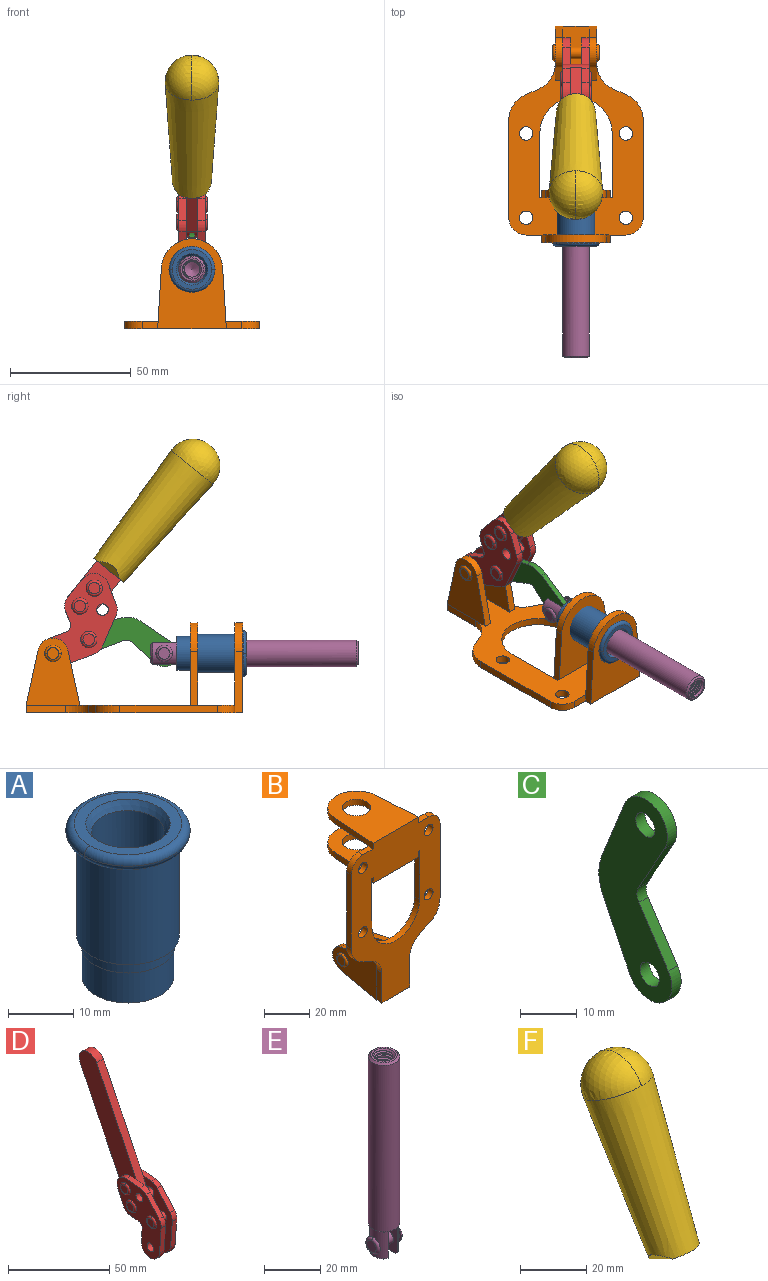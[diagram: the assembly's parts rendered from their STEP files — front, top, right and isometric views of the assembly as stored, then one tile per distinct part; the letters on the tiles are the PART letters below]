
ASSEMBLY  parts=6 mates=6
PART A: 15 faces, bbox 20.6x20.6x28.7 mm
  f0: torus R=8.26mm, axis (0,0,1), area 56.8mm2, adj f1,f10,f12
  f1: torus R=8.26mm, axis (0,0,1), area 56.8mm2, adj f0,f6,f13
  f2: cylinder r=5.59mm len=25.91mm, axis (0,0,1), area 909.6mm2, adj f3,f4
  f3: cone r=6.86mm half-angle=45deg, axis (0,0,-1), area 70.2mm2, adj f2,f14
  f4: cone r=6.47mm half-angle=30deg, axis (0,0,1), area 66.7mm2, adj f2,f13
  f5: cylinder r=7.04mm len=14.07mm, axis (0,0,1), area 252.6mm2, adj f11,f14
  f6: torus R=8.26mm, axis (0,0,1), area 56.8mm2, adj f1,f12,f13
  f7: cylinder r=7.16mm len=14.33mm, axis (0,0,1), area 91.5mm2, adj f9,f11
  f8: cylinder r=7.86mm len=18.42mm, axis (0,0,1), area 909.6mm2, adj f9,f10
  f9: plane 15.72x15.72mm, normal (0,0,-1), area 33mm2, adj f7,f8
  f10: plane 16.51x16.51mm, normal (0,0,-1), area 19.9mm2, adj f0,f8,f12
  f11: plane 14.33x14.33mm, normal (0,0,-1), area 5.7mm2, adj f5,f7
  f12: torus R=8.26mm, axis (0,0,1), area 56.8mm2, adj f0,f6,f10
  f13: plane 16.51x16.51mm, normal (0,0,1), area 82.7mm2, adj f1,f4,f6
  f14: plane 14.07x14.07mm, normal (0,0,-1), area 7.8mm2, adj f3,f5
PART B: 55 faces, bbox 55.7x37.4x89.8 mm
  f0: torus R=2.41mm, axis (-1,0,0), area 15mm2, adj f11,f15,f25
  f1: torus R=2.41mm, axis (-1,0,0), area 15mm2, adj f10,f12,f22
  f2: cylinder r=2.78mm len=5.56mm, axis (0,-1,0), area 54.2mm2, adj f30,f54
  f3: cylinder r=14.99mm len=29.97mm, axis (0,-1,0), area 145.9mm2, adj f30,f49,f53,f54
  f4: cylinder r=2.78mm len=5.56mm, axis (0,-1,0), area 54.2mm2, adj f30,f54
  f5: cylinder r=2.78mm len=5.56mm, axis (0,-1,0), area 54.2mm2, adj f30,f54
  f6: cylinder r=2.78mm len=5.56mm, axis (0,-1,0), area 54.2mm2, adj f30,f54
  f7: cylinder r=6.35mm len=12.7mm, axis (0,0,1), area 123.6mm2, adj f27,f51
  f8: cylinder r=6.35mm len=12.7mm, axis (0,0,-1), area 124.7mm2, adj f21,f35
  f9: cylinder r=2.41mm len=11.18mm, axis (-1,0,0), area 169.4mm2, adj f16,f19
  f10: plane 4.83x4.83mm, normal (1,0,0), area 18.3mm2, adj f1,f12
  f11: plane 4.83x4.83mm, normal (-1,0,0), area 18.3mm2, adj f0,f15
  f12: torus R=2.41mm, axis (-1,0,0), area 15mm2, adj f1,f10,f22
  f13: cylinder r=6.35mm len=12.41mm, axis (1,0,0), area 53.4mm2, adj f18,f19,f22,f23
  f14: cylinder r=6.35mm len=12.41mm, axis (-1,0,0), area 53.4mm2, adj f16,f17,f24,f25
  f15: torus R=2.41mm, axis (-1,0,0), area 15mm2, adj f0,f11,f25
  f16: plane 27.86x22.35mm, normal (1,0,0), area 425.4mm2, adj f9,f14,f17,f24,f30
  f17: plane 22.86x4.97mm, normal (0,0.21,0.98), area 72.5mm2, adj f14,f16,f25,f30
  f18: plane 22.86x4.97mm, normal (0,0.21,0.98), area 72.5mm2, adj f13,f19,f22,f30
  f19: plane 27.86x22.35mm, normal (-1,0,0), area 425.4mm2, adj f9,f13,f18,f23,f30
  f20: cylinder r=12.7mm len=25.35mm, axis (0,0,-1), area 119.8mm2, adj f21,f34,f35,f36
  f21: plane 34.21x28.07mm, normal (0,0,-1), area 702.4mm2, adj f8,f20,f30,f34,f36
  f22: plane 27.96x22.45mm, normal (1,0,0), area 407.2mm2, adj f1,f12,f13,f18,f23,f30,f42,f43
  f23: plane 22.86x4.97mm, normal (0,0.21,-0.98), area 72.5mm2, adj f13,f19,f22,f44
  f24: plane 22.86x4.97mm, normal (0,0.21,-0.98), area 72.5mm2, adj f14,f16,f25,f44
  f25: plane 27.86x22.35mm, normal (-1,0,0), area 407.1mm2, adj f0,f14,f15,f17,f24,f30,f45,f46
  f26: plane 3.1x0.95mm, normal (0,0,-1), area 2.7mm2, adj f30,f49,f50,f54
  f27: plane 34.21x28.07mm, normal (0,0,1), area 702.4mm2, adj f7,f28,f30,f50,f52
  f28: cylinder r=12.7mm len=25.35mm, axis (0,0,1), area 118.8mm2, adj f27,f50,f51,f52
  f29: plane 3.1x0.95mm, normal (0,0,-1), area 2.7mm2, adj f30,f52,f53,f54
  f30: plane 86.54x55.63mm, normal (0,1,0), area 2362.9mm2, adj f2,f3,f4,f5,f6,f16,f17,f18
  f31: plane 40.56x3.1mm, normal (-1,0,0), area 125.7mm2, adj f30,f32,f48,f54
  f32: cylinder r=7.11mm len=7.11mm, axis (0,-1,0), area 34.6mm2, adj f30,f31,f33,f54
  f33: plane 6.67x3.1mm, normal (0,0,1), area 20.4mm2, adj f30,f32,f34,f54
  f34: plane 25.39x3.13mm, normal (-1,0.06,0), area 79.5mm2, adj f20,f21,f33,f35,f54
  f35: plane 37.31x28.45mm, normal (0,0,1), area 789.9mm2, adj f8,f20,f34,f36,f54
  f36: plane 25.39x3.13mm, normal (1,0.06,0), area 79.5mm2, adj f20,f21,f35,f37,f54
  f37: plane 6.67x3.1mm, normal (0,0,1), area 20.4mm2, adj f30,f36,f38,f54
  f38: cylinder r=7.11mm len=7.11mm, axis (0,-1,0), area 34.6mm2, adj f30,f37,f39,f54
  f39: plane 40.56x3.1mm, normal (1,0,0), area 125.7mm2, adj f30,f38,f40,f54
  f40: cylinder r=11.18mm len=10.16mm, axis (0,-1,0), area 39.5mm2, adj f30,f39,f41,f54
  f41: plane 6.09x3.1mm, normal (0.42,0,-0.91), area 20.8mm2, adj f30,f40,f42,f54
  f42: cylinder r=11.18mm len=9.41mm, axis (0,-1,0), area 37.2mm2, adj f22,f30,f41,f43,f54
  f43: plane 16.5x3.1mm, normal (1,0,0), area 51.1mm2, adj f22,f42,f44,f54
  f44: plane 17.37x3.1mm, normal (0,0,-1), area 53.8mm2, adj f23,f24,f30,f43,f45,f54
  f45: plane 16.5x3.1mm, normal (-1,0,0), area 51.1mm2, adj f25,f44,f46,f54
  f46: cylinder r=11.18mm len=9.41mm, axis (0,-1,0), area 37.2mm2, adj f25,f30,f45,f47,f54
  f47: plane 6.09x3.1mm, normal (-0.42,0,-0.91), area 20.8mm2, adj f30,f46,f48,f54
  f48: cylinder r=11.18mm len=10.16mm, axis (0,-1,0), area 39.5mm2, adj f30,f31,f47,f54
  f49: plane 26.54x3.1mm, normal (-1,0,0), area 82.3mm2, adj f3,f26,f30,f54
  f50: plane 25.39x3.1mm, normal (1,0.06,0), area 78.8mm2, adj f26,f27,f28,f51,f54
  f51: plane 37.31x28.45mm, normal (0,0,-1), area 789.9mm2, adj f7,f28,f50,f52,f54
  f52: plane 25.39x3.1mm, normal (-1,0.06,0), area 78.8mm2, adj f27,f28,f29,f51,f54
  f53: plane 26.54x3.1mm, normal (1,0,0), area 82.3mm2, adj f3,f29,f30,f54
  f54: plane 89.66x55.63mm, normal (0,-1,0), area 2678.5mm2, adj f2,f3,f4,f5,f6,f26,f29,f31
PART C: 12 faces, bbox 2.3x18.2x42.8 mm
  f0: cylinder r=2.4mm len=4.8mm, axis (1,0,0), area 34.9mm2, adj f4,f11
  f1: cylinder r=10.41mm len=8.47mm, axis (1,0,0), area 20.2mm2, adj f4,f9,f10,f11
  f2: cylinder r=3.05mm len=3.16mm, axis (1,0,0), area 7.7mm2, adj f4,f6,f7,f11
  f3: cylinder r=2.4mm len=4.8mm, axis (1,0,0), area 34.9mm2, adj f4,f11
  f4: plane 42.81x18.23mm, normal (-1,0,0), area 414.1mm2, adj f0,f1,f2,f3,f5,f6,f7,f8
  f5: cylinder r=5.54mm len=10.67mm, axis (1,0,0), area 41.8mm2, adj f4,f6,f10,f11
  f6: plane 11.66x6.53mm, normal (0,-0.87,-0.49), area 30.9mm2, adj f2,f4,f5,f11
  f7: plane 11.17x7.33mm, normal (0,-0.84,0.55), area 30.9mm2, adj f2,f4,f8,f11
  f8: cylinder r=5.54mm len=10.51mm, axis (1,0,0), area 41.8mm2, adj f4,f7,f9,f11
  f9: plane 13.67x6.67mm, normal (0,0.9,-0.44), area 35.1mm2, adj f1,f4,f8,f11
  f10: plane 14.1x5.7mm, normal (0,0.93,0.37), area 35.1mm2, adj f1,f4,f5,f11
  f11: plane 42.81x18.23mm, normal (1,0,0), area 414.1mm2, adj f0,f1,f2,f3,f5,f6,f7,f8
PART D: 59 faces, bbox 12.9x60.2x99.6 mm
  f0: torus R=2.39mm, axis (-1,0,0), area 14.9mm2, adj f20,f43,f51
  f1: torus R=2.39mm, axis (-1,0,0), area 14.9mm2, adj f19,f42,f51
  f2: torus R=2.39mm, axis (-1,0,0), area 14.9mm2, adj f18,f35,f51
  f3: torus R=2.39mm, axis (-1,0,0), area 14.9mm2, adj f14,f17,f23
  f4: torus R=2.39mm, axis (-1,0,0), area 14.9mm2, adj f13,f16,f23
  f5: torus R=2.39mm, axis (-1,0,0), area 14.9mm2, adj f12,f15,f23
  f6: cylinder r=2.39mm len=4.78mm, axis (1,0,0), area 46.5mm2, adj f48,f50,f51
  f7: cylinder r=2.39mm len=4.78mm, axis (1,0,0), area 46.5mm2, adj f50,f51
  f8: cylinder r=6.35mm len=12.68mm, axis (1,0,0), area 61.8mm2, adj f38,f39,f50,f51
  f9: cylinder r=2.39mm len=4.78mm, axis (-1,0,0), area 70.5mm2, adj f46,f50
  f10: cylinder r=2.39mm len=4.78mm, axis (-1,0,0), area 46.5mm2, adj f23,f45,f46
  f11: cylinder r=2.39mm len=4.78mm, axis (-1,0,0), area 46.5mm2, adj f23,f46
  f12: plane 4.78x4.78mm, normal (1,0,0), area 17.9mm2, adj f5,f15
  f13: plane 4.78x4.78mm, normal (1,0,0), area 17.9mm2, adj f4,f16
  f14: plane 4.78x4.78mm, normal (1,0,0), area 17.9mm2, adj f3,f17
  f15: torus R=2.39mm, axis (-1,0,0), area 14.9mm2, adj f5,f12,f23
  f16: torus R=2.39mm, axis (-1,0,0), area 14.9mm2, adj f4,f13,f23
  f17: torus R=2.39mm, axis (-1,0,0), area 14.9mm2, adj f3,f14,f23
  f18: plane 4.78x4.78mm, normal (-1,0,0), area 17.9mm2, adj f2,f35
  f19: plane 4.78x4.78mm, normal (-1,0,0), area 17.9mm2, adj f1,f42
  f20: plane 4.78x4.78mm, normal (-1,0,0), area 17.9mm2, adj f0,f43
  f21: plane 2.26x0.2mm, normal (1,0,0), area 0.2mm2, adj f31,f44
  f22: plane 2.26x0.2mm, normal (-1,0,0), area 0.2mm2, adj f41,f44
  f23: plane 39.37x30.77mm, normal (1,0,0), area 565.5mm2, adj f3,f4,f5,f10,f11,f15,f16,f17
  f24: cylinder r=6.1mm len=4.15mm, axis (-1,0,0), area 14.7mm2, adj f23,f25,f32,f46
  f25: plane 10.25x9.01mm, normal (0,-0.75,0.66), area 42.3mm2, adj f23,f24,f26,f46
  f26: cylinder r=6.35mm len=4.64mm, axis (-1,0,0), area 15.6mm2, adj f23,f25,f27,f46
  f27: plane 15.84x3.1mm, normal (0,-1,-0.07), area 49.2mm2, adj f23,f26,f28,f46
  f28: cylinder r=6.35mm len=12.68mm, axis (-1,0,0), area 61.8mm2, adj f23,f27,f29,f46
  f29: plane 8.11x3.1mm, normal (0,1,0.07), area 25.2mm2, adj f23,f28,f30,f46
  f30: cylinder r=3.05mm len=3.25mm, axis (-1,0,0), area 14.8mm2, adj f23,f29,f31,f46
  f31: plane 5.99x3.1mm, normal (0,0.07,-1), area 18.6mm2, adj f21,f23,f30,f44,f46
  f32: plane 9.5x3.1mm, normal (0,-0.07,1), area 29.5mm2, adj f23,f24,f33,f46,f47
  f33: cylinder r=6.1mm len=8.63mm, axis (-1,0,0), area 39.1mm2, adj f23,f32,f34,f47
  f34: plane 8.65x3.96mm, normal (0,0.91,-0.42), area 29.5mm2, adj f23,f33,f44,f47
  f35: torus R=2.39mm, axis (-1,0,0), area 14.9mm2, adj f2,f18,f51
  f36: plane 10.25x9.01mm, normal (0,-0.75,0.66), area 42.3mm2, adj f37,f49,f50,f51
  f37: cylinder r=6.35mm len=4.64mm, axis (1,0,0), area 15.6mm2, adj f36,f38,f50,f51
  f38: plane 15.84x3.1mm, normal (0,-1,-0.07), area 49.2mm2, adj f8,f37,f50,f51
  f39: plane 8.11x3.1mm, normal (0,1,0.07), area 25.2mm2, adj f8,f40,f50,f51
  f40: cylinder r=3.05mm len=3.25mm, axis (1,0,0), area 14.8mm2, adj f39,f41,f50,f51
  f41: plane 5.99x3.1mm, normal (0,0.07,-1), area 18.6mm2, adj f22,f40,f44,f50,f51
  f42: torus R=2.39mm, axis (-1,0,0), area 14.9mm2, adj f1,f19,f51
  f43: torus R=2.39mm, axis (-1,0,0), area 14.9mm2, adj f0,f20,f51
  f44: cylinder r=6.35mm len=12.12mm, axis (-1,0,0), area 128.9mm2, adj f21,f22,f23,f31,f34,f41,f46,f47
  f45: plane 2.65x1.35mm, normal (1,0,0), area 1mm2, adj f10,f55
  f46: plane 39.08x20.42mm, normal (-1,0,0), area 412.5mm2, adj f9,f10,f11,f24,f25,f26,f27,f28
  f47: plane 77.62x39.82mm, normal (1,0,0), area 850mm2, adj f32,f33,f34,f44,f53,f54,f55
  f48: plane 2.65x1.35mm, normal (-1,0,0), area 1mm2, adj f6,f55
  f49: cylinder r=6.1mm len=4.15mm, axis (1,0,0), area 14.7mm2, adj f36,f50,f51,f56
  f50: plane 39.08x20.42mm, normal (1,0,0), area 412.5mm2, adj f6,f7,f8,f9,f36,f37,f38,f39
  f51: plane 39.37x30.77mm, normal (-1,0,0), area 565.5mm2, adj f0,f1,f2,f6,f7,f8,f35,f36
  f52: plane 8.65x3.96mm, normal (0,0.91,-0.42), area 29.5mm2, adj f44,f51,f57,f58
  f53: plane 68.49x33.4mm, normal (0,0.9,-0.44), area 358.1mm2, adj f44,f47,f54,f58
  f54: cylinder r=6.35mm len=12.06mm, axis (1,0,0), area 93.7mm2, adj f47,f53,f55,f58
  f55: plane 68.49x33.4mm, normal (0,-0.9,0.44), area 358.1mm2, adj f44,f45,f46,f47,f48,f50,f54,f58
  f56: plane 9.5x3.1mm, normal (0,-0.07,1), area 29.5mm2, adj f49,f50,f51,f57,f58
  f57: cylinder r=6.1mm len=8.63mm, axis (1,0,0), area 39.1mm2, adj f51,f52,f56,f58
  f58: plane 77.62x39.82mm, normal (-1,0,0), area 850mm2, adj f44,f52,f53,f54,f55,f56,f57
PART E: 48 faces, bbox 12.6x11.1x86.1 mm
  f0: torus R=2.41mm, axis (-1,0,0), area 15mm2, adj f30,f32,f34
  f1: torus R=2.41mm, axis (-1,0,0), area 15mm2, adj f29,f31,f33
  f2: cylinder r=5.54mm len=72.39mm, axis (0,0,1), area 2518.5mm2, adj f3,f4,f42,f43
  f3: cone r=5.54mm half-angle=45deg, axis (0,0,1), area 7.6mm2, adj f2,f5,f41
  f4: cone r=5.54mm half-angle=45deg, axis (0,0,-1), area 34.9mm2, adj f2,f39
  f5: cylinder r=5.08mm len=11.48mm, axis (0,0,1), area 108.3mm2, adj f3,f7,f8,f41
  f6: cylinder r=2.41mm len=4.83mm, axis (-1,0,0), area 71.2mm2, adj f40,f41
  f7: cylinder r=2.41mm len=4.83mm, axis (-1,0,0), area 7.6mm2, adj f5,f34
  f8: cone r=5.08mm half-angle=45deg, axis (0,0,1), area 10.6mm2, adj f5,f37,f41
  f9: cone r=3.98mm half-angle=45deg, axis (0,0,1), area 17.6mm2, adj f27,f39,f45,f46,f47
  f10: cylinder r=2.41mm len=4.83mm, axis (-1,0,0), area 7.6mm2, adj f33,f38
  f11: cylinder r=3.2mm len=6.4mm, axis (0,0,1), area 78.4mm2, adj f12,f28,f44,f45,f47
  f12: cylinder r=3.2mm len=6.4mm, axis (0,0,1), area 10.5mm2, adj f11,f13,f45,f47
  f13: cylinder r=3.2mm len=6.4mm, axis (0,0,1), area 10.5mm2, adj f12,f14,f45,f47
  f14: cylinder r=3.2mm len=6.4mm, axis (0,0,1), area 10.5mm2, adj f13,f15,f45,f47
  f15: cylinder r=3.2mm len=6.4mm, axis (0,0,1), area 10.5mm2, adj f14,f16,f45,f47
  f16: cylinder r=3.2mm len=6.4mm, axis (0,0,1), area 10.5mm2, adj f15,f17,f45,f47
  f17: cylinder r=3.2mm len=6.4mm, axis (0,0,1), area 10.5mm2, adj f16,f18,f45,f47
  f18: cylinder r=3.2mm len=6.4mm, axis (0,0,1), area 10.5mm2, adj f17,f19,f45,f47
  f19: cylinder r=3.2mm len=6.4mm, axis (0,0,1), area 10.5mm2, adj f18,f20,f45,f47
  f20: cylinder r=3.2mm len=6.4mm, axis (0,0,1), area 10.5mm2, adj f19,f21,f45,f47
  f21: cylinder r=3.2mm len=6.4mm, axis (0,0,1), area 10.5mm2, adj f20,f22,f45,f47
  f22: cylinder r=3.2mm len=6.4mm, axis (0,0,1), area 10.5mm2, adj f21,f23,f45,f47
  f23: cylinder r=3.2mm len=6.4mm, axis (0,0,1), area 10.5mm2, adj f22,f24,f45,f47
  f24: cylinder r=3.2mm len=6.4mm, axis (0,0,1), area 10.5mm2, adj f23,f25,f45,f47
  f25: cylinder r=3.2mm len=6.4mm, axis (0,0,1), area 10.5mm2, adj f24,f26,f45,f47
  f26: cylinder r=3.2mm len=6.4mm, axis (0,0,1), area 10.5mm2, adj f25,f27,f45,f47
  f27: cylinder r=3.2mm len=6.4mm, axis (0,0,1), area 7.4mm2, adj f9,f26,f45,f47
  f28: cone r=3.2mm half-angle=60deg, axis (0,0,1), area 37.2mm2, adj f11
  f29: plane 4.83x4.83mm, normal (-1,0,0), area 18.3mm2, adj f1,f31
  f30: plane 4.83x4.83mm, normal (1,0,0), area 18.3mm2, adj f0,f32
  f31: torus R=2.41mm, axis (-1,0,0), area 15mm2, adj f1,f29,f33
  f32: torus R=2.41mm, axis (-1,0,0), area 15mm2, adj f0,f30,f34
  f33: plane 6.83x6.83mm, normal (1,0,0), area 18.3mm2, adj f1,f10,f31
  f34: plane 6.83x6.83mm, normal (-1,0,0), area 18.3mm2, adj f0,f7,f32
  f35: cone r=5.08mm half-angle=45deg, axis (0,0,1), area 10.6mm2, adj f36,f38,f40
  f36: plane 7.25x1.97mm, normal (0,0,-1), area 10mm2, adj f35,f40
  f37: plane 7.25x1.97mm, normal (0,0,-1), area 10mm2, adj f8,f41
  f38: cylinder r=5.08mm len=11.48mm, axis (0,0,1), area 108.3mm2, adj f10,f35,f40,f42
  f39: plane 9.55x9.55mm, normal (0,0,1), area 22mm2, adj f4,f9
  f40: plane 12.76x10.09mm, normal (1,0,0), area 95.7mm2, adj f6,f35,f36,f38,f42,f43
  f41: plane 12.76x10.09mm, normal (-1,0,0), area 95.7mm2, adj f3,f5,f6,f8,f37,f43
  f42: cone r=5.54mm half-angle=45deg, axis (0,0,1), area 7.6mm2, adj f2,f38,f40
  f43: plane 11.07x4.7mm, normal (0,0,-1), area 50.4mm2, adj f2,f40,f41
  f44: plane 0.89x0.62mm, normal (-1,0,0), area 0.3mm2, adj f11,f45,f46,f47
  f45: bspline ~24.8x7.63mm, area 266.6mm2, adj f9,f11,f12,f13,f14,f15,f16,f17
  f46: bspline ~24.87x7.63mm, area 73.6mm2, adj f9,f44,f45,f47
  f47: bspline ~24.98x7.63mm, area 272.5mm2, adj f9,f11,f12,f13,f14,f15,f16,f17
PART F: 11 faces, bbox 22.3x42.6x64.5 mm
  f0: sphere r=11.13mm, area 411.4mm2, adj f1,f8
  f1: cone r=11.11mm half-angle=3.3deg, axis (0,0.44,0.9), area 3251.8mm2, adj f0,f7,f8,f9,f10
  f2: cylinder r=6.16mm len=11.7mm, axis (1,0,0), area 89.5mm2, adj f3,f4,f5,f6
  f3: plane 60.23x36.75mm, normal (-1,0,0), area 763.6mm2, adj f2,f4,f6,f10
  f4: plane 51.37x25.05mm, normal (0,0.9,-0.44), area 264.2mm2, adj f2,f3,f5,f10
  f5: plane 60.23x36.75mm, normal (1,0,0), area 763.6mm2, adj f2,f4,f6,f10
  f6: plane 51.37x25.05mm, normal (0,-0.9,0.44), area 264.2mm2, adj f2,f3,f5,f10
  f7: plane 9.95x5.95mm, normal (0.71,-0.31,-0.64), area 25.8mm2, adj f1,f10
  f8: sphere r=11.13mm, area 411.4mm2, adj f0,f1
  f9: plane 9.95x5.95mm, normal (-0.71,-0.31,-0.64), area 25.8mm2, adj f1,f10
  f10: plane 14.27x11.38mm, normal (0,-0.44,-0.9), area 106.7mm2, adj f1,f3,f4,f5,f6,f7,f9
PLACE A rot(axis=(1,0,0),90deg) t=(0,10.16,0)mm
PLACE B rot(axis=(1,0,0),90deg) t=(0,9.14,0)mm fixed
PLACE C rot(axis=(1,0,0),102.4deg) t=(0,15.57,3.88)mm
PLACE D rot(axis=(1,0,0),64.9deg) t=(0,1.73,15.92)mm
PLACE E rot(axis=(1,0,0),90deg) t=(0,10.66,0)mm
PLACE F rot(axis=(1,0,0),64.9deg) t=(-0.04,1.73,15.92)mm
MATE fastened F.f2 <-> D.f54  axis (1,0,0) through (-2.35,-17.78,103.47)mm
MATE revolute C.f5 <-> E.f6  axis (1,0,0) through (0,-4.81,24.61)mm
MATE fastened A.f2 <-> B.f7  axis (0,1,0) through (0,-37.25,24.61)mm
MATE revolute C.f3 <-> D.f4  axis (1,0,0) through (0,26.42,30.32)mm
MATE revolute D.f7 <-> B.f0  axis (-1,0,0) through (0,41.23,24.61)mm
MATE slider E.f2 <-> A.f2  axis (0,-1,0) through (0,-48.12,24.61)mm
